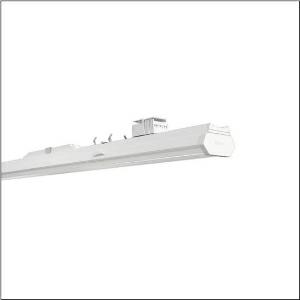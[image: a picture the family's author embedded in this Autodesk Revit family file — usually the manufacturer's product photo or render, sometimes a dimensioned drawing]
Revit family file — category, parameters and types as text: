
# Revit family: licross_r__21_protected_mo_52tp12dn4a5g3s_7eca
name_source: partatom
category: Lighting Fixtures
units: mm (PartAtom-declared; Revit-internal decimal feet)

## family parameters
Cut with Voids When Loaded = No
Host = Face
Light Source = No
Part Type = Normal
Room Calculation Point = No
Round Connector Dimension = Use Diameter
Shared = No

## types (1)
- --- (1 x LED, 940 lm, 6.8 W, 4000K)
    Apparent Load = 7 VA
    CIE Flux Codes = 73 92 98 99 100
    Color Rendering = 80
    Color Temperature = 4000K
    Default Elevation = 1800 mm
    Description = Licross® 21 Protected MO, luminaire insert, of sheet steel, galvanised, coil coated, white, length: 1.500mm, width: 90mm, height: 103mm, LED rated luminous flux: 10.700lm, light colour: 840, control gear: DALI 2 (for two DALI lines), with plug, 6-pole, with phase selection, for trunking rail, 14-core, mains connection: 220..240V, AC, 50/60Hz, rated input power: 66W, for trunking rail, 14-core, halogen-free wiring, for emergency light function, converter,control gear: single battery element, battery: LiFePO4, 9Ah, primary light control with lens, of plastic, primary optical cover: cover, of PMMA, light emission: direct distribution, primary light characteristic: symmetric, protection rating (complete): IP64, insulation class (complete): insulation class I (protective earthing), certification: CE, UKCA, protection symbol: D if used in an environment with conductive dust loads with corresponding accessories, impact resistance: IK06, permissible ambient temperature for indoor applications: +5..+35°C, standard: EN 60598-2-22, LABS conformity tested according to VDMA 24364:2018-05, reducing of maximum allowable ambient temperature of 5°C with ceiling mounting, corresponds to IFS (International Featured Standards) requirements for safety and quality in the food industry, packaging unit: 1 piece
    Height = 92 mm
    Lamp = 1 x LED
    Lamp Light Flux = 940 lm
    Lamp Power = 6.8 W
    Lamp count = 1
    Length = 1500 mm
    Luminous efficacy = 138 lm/W
    Manufacturer = Siteco
    ModVariant = No
    Model = 52TP12DN4A5G3S
    Mounting Place = Ceiling
    Mounting Type = Pendant
    Number of Poles = 1
    OnlyDefault = Yes
    Power Factor = 1
    Product Name = Licross® 21 Protected MO
    Product group = luminaire insert
    ProductGroupID = 902
    Protection Class = Protection class I
    Protection Degree = IP 64
    RLX_Detail_Level = 1
    RLX_Emergency_Light_Flux = 0 lm
    RLX_Emergency_Type = 0
    RLX_Emergency_Type_DB = No
    RlxData = <blob elided: 24897 chars, md5=3dd036b6>
    Socket = socket
    Standby Power = 0 W
    System Light Flux = 940 lm
    System Power = 7 W
    Type Comments = : emergency light operation: 3 h
    Type Image = l_1256148.jpg
    URL = http://relux.com
    VarID = @adj_110934
    Voltage = 0 V
    Weight = 0.00 kg
    Width = 88 mm

## geometry (parser evidence)
native form markers: Blend x4, Sweep x11
no freeform markers — native parametric forms only
